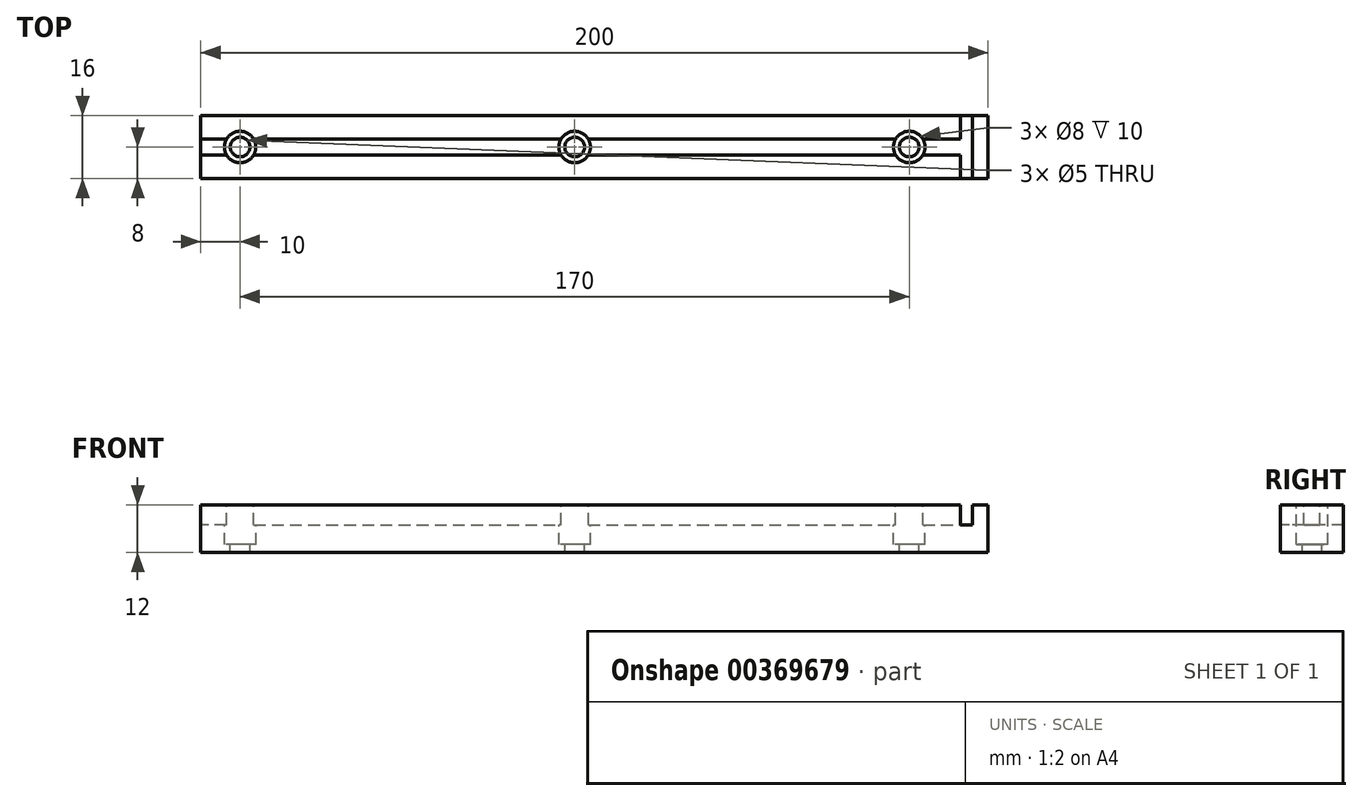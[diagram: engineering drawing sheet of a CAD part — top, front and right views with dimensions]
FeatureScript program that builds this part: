
annotation { "Feature Type Name" : "Feature", "Feature Type Description" : "" }
export const myFeature = defineFeature(function(context is Context, id is Id, definition is map)
    precondition{}
    {
        {
            var Q0;
            Q0=qCreatedBy(makeId("Top.planeOp"),FACE);
            var sketch = newSketch(context, id + "F0", { "sketchPlane" : qUnion([Q0])});
            skLineSegment(sketch, "E0.bottom", {"start": v(0, 0) * mm, "end": v(-200, 0) * mm});
            skLineSegment(sketch, "E0.top", {"start": v(0, 16) * mm, "end": v(-200, 16) * mm});
            skLineSegment(sketch, "E0.left", {"start": v(0, 0) * mm, "end": v(0, 16) * mm});
            skLineSegment(sketch, "E0.right", {"start": v(-200, 0) * mm, "end": v(-200, 16) * mm});
            skSolve(sketch);
        }
        {
            var Q0;
            Q0=makeQuery(id+"F0.imprint","IMPRINT",FACE,{"disambiguationData":[TD([[makeQuery(id+"F0.imprint","IMPRINT",EDGE,{"derivedFrom":sQuery(id+"F0.wireOp",EDGE,"E0.bottom")}),-1.0]])]});
            extrude(context, id + "F1", {"entities" : qUnion([Q0]), "depth" : 12 * mm});
        }
        {
            var Q0;
            Q0=makeQuery(id+"F1.opExtrude","CAP_FACE",FACE,{"disambiguationData":[OSD([sQuery(id+"F0.wireOp",EDGE,"E0.bottom"),sQuery(id+"F0.wireOp",EDGE,"E0.top"),sQuery(id+"F0.wireOp",EDGE,"E0.left"),sQuery(id+"F0.wireOp",EDGE,"E0.right")])],"isStart":false});
            var sketch = newSketch(context, id + "F2", { "sketchPlane" : qUnion([Q0])});
            skLineSegment(sketch, "E1.0.0", {"start": v(0, 0) * mm, "end": v(0, 16) * mm});
            skLineSegment(sketch, "E1.0.1", {"start": v(0, 16) * mm, "end": v(-200, 16) * mm});
            skLineSegment(sketch, "E1.0.2", {"start": v(-200, 16) * mm, "end": v(-200, 0) * mm});
            skLineSegment(sketch, "E1.0.3", {"start": v(-200, 0) * mm, "end": v(0, 0) * mm});
            skLineSegment(sketch, "E2", {"start": v(-200, 10) * mm, "end": v(-4, 10) * mm});
            skLineSegment(sketch, "E3", {"start": v(-4, 10) * mm, "end": v(-4, 6) * mm});
            skLineSegment(sketch, "E4", {"start": v(-4, 6) * mm, "end": v(-200, 6) * mm});
            skSolve(sketch);
        }
        {
            var Q0;
            {var subQ0=sQuery(id+"F2.wireOp",EDGE,"E2");Q0=makeQuery(id+"F2.imprint","IMPRINT",FACE,{"disambiguationData":[TD([[makeQuery(id+"F2.imprint","IMPRINT",EDGE,{"derivedFrom":subQ0}),-1.0]])]});}
            extrude(context, id + "F3", {"entities" : qUnion([Q0]), "operationType" : NewBodyOperationType.REMOVE, "oppositeDirection" : true, "depth" : 5 * mm});
        }
        {
            var Q0;
            Q0=makeQuery(id+"F1.opExtrude","CAP_FACE",FACE,{"disambiguationData":[OSD([sQuery(id+"F0.wireOp",EDGE,"E0.bottom"),sQuery(id+"F0.wireOp",EDGE,"E0.top"),sQuery(id+"F0.wireOp",EDGE,"E0.left"),sQuery(id+"F0.wireOp",EDGE,"E0.right")])],"isStart":false});
            var sketch = newSketch(context, id + "F4", { "sketchPlane" : qUnion([Q0])});
            skCircle(sketch, "E5", {"center": v(-190, 8) * mm, "radius": 4 * mm});
            skCircle(sketch, "E6", {"center": v(-105, 8) * mm, "radius": 4 * mm});
            skCircle(sketch, "E7", {"center": v(-20, 8) * mm, "radius": 4 * mm});
            skSolve(sketch);
        }
        {
            var Q0;
            Q0 = qSketchRegion(id + "F4", true);
            extrude(context, id + "F5", {"entities" : qUnion([Q0]), "operationType" : NewBodyOperationType.REMOVE, "oppositeDirection" : true, "depth" : 10 * mm});
        }
        {
            var Q0;
            Q0=makeQuery(id+"F1.opExtrude","CAP_FACE",FACE,{"disambiguationData":[OSD([sQuery(id+"F0.wireOp",EDGE,"E0.bottom"),sQuery(id+"F0.wireOp",EDGE,"E0.top"),sQuery(id+"F0.wireOp",EDGE,"E0.left"),sQuery(id+"F0.wireOp",EDGE,"E0.right")])],"isStart":false});
            var sketch = newSketch(context, id + "F6", { "sketchPlane" : qUnion([Q0])});
            skCircle(sketch, "E8.0.0", {"center": v(-190, 8) * mm, "radius": 4 * mm});
            skCircle(sketch, "E9.0.0", {"center": v(-105, 8) * mm, "radius": 4 * mm});
            skCircle(sketch, "E10.0.0", {"center": v(-20, 8) * mm, "radius": 4 * mm});
            skSolve(sketch);
        }
        {
            var Q0;
            Q0=sQuery(id+"F6.wireOp",VERTEX,"E9.0.0.center");
            var Q1;
            Q1=sQuery(id+"F6.wireOp",VERTEX,"E8.0.0.center");
            var Q2;
            Q2=sQuery(id+"F6.wireOp",VERTEX,"E10.0.0.center");
            var Q3;
            Q3=makeQuery(id+"F1.opExtrude","SWEPT_BODY",BODY,{"disambiguationData":[OSD([sQuery(id+"F0.wireOp",EDGE,"E0.bottom"),sQuery(id+"F0.wireOp",EDGE,"E0.top"),sQuery(id+"F0.wireOp",EDGE,"E0.left"),sQuery(id+"F0.wireOp",EDGE,"E0.right")])]});
            hole(context, id + "F7", {"style" : HoleStyle.SIMPLE, "endStyle" : HoleEndStyle.THROUGH, "holeDiameter" : 5 * mm, "isTappedThrough" : true, "tappedDepth" : 12 * mm, "tapClearance" : 3, "locations" : qUnion([Q0, Q1, Q2]), "scope" : qUnion([Q3])});
        }
        {
            var Q0;
            Q0=makeQuery(id+"F1.opExtrude","CAP_FACE",FACE,{"disambiguationData":[OSD([sQuery(id+"F0.wireOp",EDGE,"E0.bottom"),sQuery(id+"F0.wireOp",EDGE,"E0.top"),sQuery(id+"F0.wireOp",EDGE,"E0.left"),sQuery(id+"F0.wireOp",EDGE,"E0.right")])],"isStart":false});
            var sketch = newSketch(context, id + "F8", { "sketchPlane" : qUnion([Q0])});
            skLineSegment(sketch, "E11.bottom", {"start": v(-4, 16) * mm, "end": v(-7, 16) * mm});
            skLineSegment(sketch, "E11.top", {"start": v(-4, 0) * mm, "end": v(-7, 0) * mm});
            skLineSegment(sketch, "E11.left", {"start": v(-4, 16) * mm, "end": v(-4, 0) * mm});
            skLineSegment(sketch, "E11.right", {"start": v(-7, 16) * mm, "end": v(-7, 0) * mm});
            skArc(sketch, "E12.0.0", {"start": v(-16.54, 10) * mm, "mid": v(-16, 8) * mm, "end": v(-16.54, 6) * mm});
            skLineSegment(sketch, "E12.0.1", {"start": v(-16.54, 6) * mm, "end": v(-4, 6) * mm});
            skLineSegment(sketch, "E12.0.2", {"start": v(-4, 6) * mm, "end": v(-4, 10) * mm});
            skLineSegment(sketch, "E12.0.3", {"start": v(-4, 10) * mm, "end": v(-16.54, 10) * mm});
            skSolve(sketch);
        }
        {
            var Q0;
            {var subQ0=sQuery(id+"F8.wireOp",EDGE,"E11.bottom");Q0=makeQuery(id+"F8.imprint","IMPRINT",FACE,{"disambiguationData":[TD([[makeQuery(id+"F8.imprint","IMPRINT",EDGE,{"derivedFrom":subQ0}),1.0]])]});}
            var Q1;
            {var subQ0=sQuery(id+"F8.wireOp",EDGE,"E11.top");Q1=makeQuery(id+"F8.imprint","IMPRINT",FACE,{"disambiguationData":[TD([[makeQuery(id+"F8.imprint","IMPRINT",EDGE,{"derivedFrom":subQ0}),-1.0]])]});}
            extrude(context, id + "F9", {"entities" : qUnion([Q0, Q1]), "operationType" : NewBodyOperationType.REMOVE, "oppositeDirection" : true, "depth" : 5 * mm});
        }
    });
